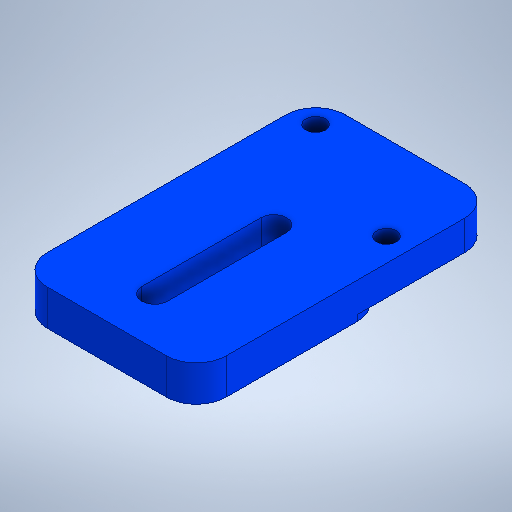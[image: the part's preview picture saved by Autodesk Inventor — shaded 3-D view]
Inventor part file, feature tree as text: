
AUTODESK INVENTOR PART (.ipt)
format: ipt  version: 2025.2 (Build 292293000, 293)  size: 270,336 bytes
history: native  units: mm
features: extrude x3, sketch x3, fillet x2
ambient origin geometry x8: Origin, YZ Plane, XZ Plane, XY Plane, X Axis, Y Axis, Z Axis, Center Point
bodies: Solid1 (feature_tree)
feature tree (8):
  extrude  "Extrusion1"  Depth=50.0mm
  fillet  "Fillet1"  Radius=5.0mm
  sketch  "Sketch2"  dims[d4=5.0mm d5=3.9mm d6=11.1mm]
  extrude  "Extrusion2"  Depth=5.0mm
  fillet  "Fillet2"  Radius=11.1mm
  extrude  "Extrusion3"  Depth=5.0mm
  sketch  "Sketch1"  dims[d0=30.0mm d1=50.0mm d2=5.0mm d3=0.0mm]
  sketch  "Sketch3"  dims[d7=22.2mm d8=10.3mm d9=3.3mm d10=3.3mm d11=8.0mm d12=4.3mm d13=20.0mm d14=4.3mm d15=32.0mm d16=1.0mm d17=0.0mm d18=5.0mm d19=0.0mm d20=0.0mm]
